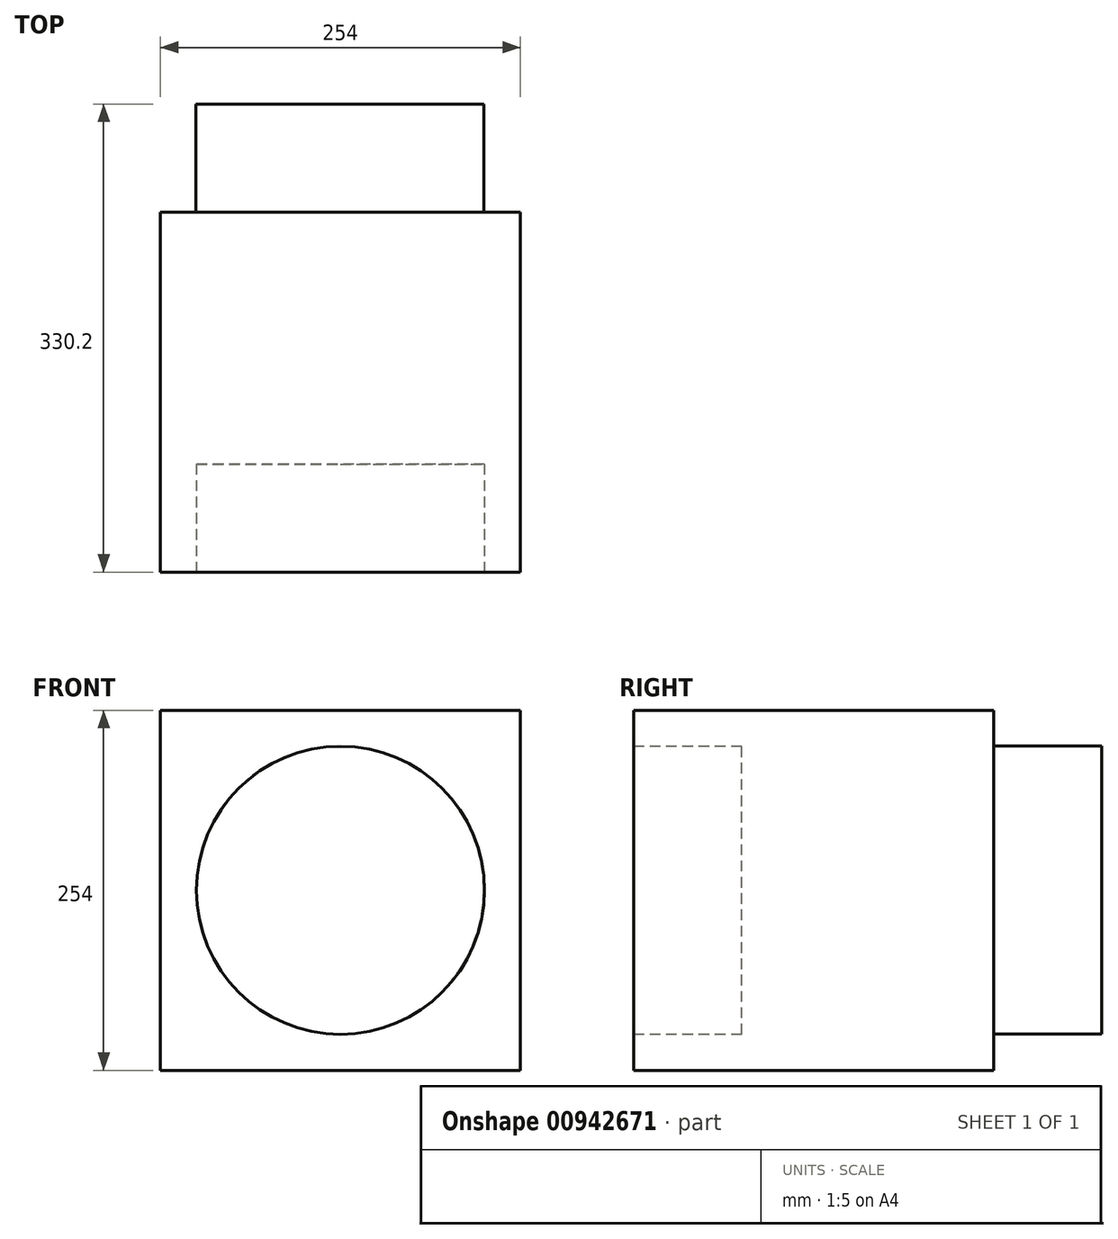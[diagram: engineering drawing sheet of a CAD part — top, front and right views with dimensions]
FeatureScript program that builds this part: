
annotation { "Feature Type Name" : "Feature", "Feature Type Description" : "" }
export const myFeature = defineFeature(function(context is Context, id is Id, definition is map)
    precondition{}
    {
        {
            var Q0;
            Q0=qCreatedBy(makeId("Front.planeOp"),FACE);
            var sketch = newSketch(context, id + "F0", { "sketchPlane" : qUnion([Q0])});
            skLineSegment(sketch, "E0.bottom", {"start": v(-127, 127) * mm, "end": v(127, 127) * mm});
            skLineSegment(sketch, "E0.top", {"start": v(-127, -127) * mm, "end": v(127, -127) * mm});
            skLineSegment(sketch, "E0.left", {"start": v(-127, 127) * mm, "end": v(-127, -127) * mm});
            skLineSegment(sketch, "E0.right", {"start": v(127, 127) * mm, "end": v(127, -127) * mm});
            skPoint(sketch, "E0.middle", {"position": v(0, 0) * mm});
            skSolve(sketch);
        }
        {
            var Q0;
            Q0 = qSketchRegion(id + "F0", true);
            extrude(context, id + "F1", {"entities" : qUnion([Q0]), "depth" : 254 * mm, "offsetDistance" : 25.4 * mm});
        }
        {
            var Q0;
            Q0=makeQuery(id+"F1.opExtrude","CAP_FACE",FACE,{"disambiguationData":[OSD([sQuery(id+"F0.wireOp",EDGE,"E0.bottom"),sQuery(id+"F0.wireOp",EDGE,"E0.top"),sQuery(id+"F0.wireOp",EDGE,"E0.left"),sQuery(id+"F0.wireOp",EDGE,"E0.right")])],"isStart":true});
            var sketch = newSketch(context, id + "F2", { "sketchPlane" : qUnion([Q0])});
            skCircle(sketch, "E1", {"center": v(0.46, 0.15) * mm, "radius": 101.6 * mm});
            skSolve(sketch);
        }
        {
            var Q0;
            Q0=makeQuery(id+"F1.opExtrude","CAP_FACE",FACE,{"disambiguationData":[OSD([sQuery(id+"F0.wireOp",EDGE,"E0.bottom"),sQuery(id+"F0.wireOp",EDGE,"E0.top"),sQuery(id+"F0.wireOp",EDGE,"E0.left"),sQuery(id+"F0.wireOp",EDGE,"E0.right")])],"isStart":false});
            var sketch = newSketch(context, id + "F3", { "sketchPlane" : qUnion([Q0])});
            skCircle(sketch, "E2", {"center": v(0, 0) * mm, "radius": 101.6 * mm});
            skSolve(sketch);
        }
        {
            var Q0;
            Q0=makeQuery(id+"F3.imprint","IMPRINT",FACE,{"disambiguationData":[TD([[makeQuery(id+"F3.imprint","IMPRINT",EDGE,{"derivedFrom":sQuery(id+"F3.wireOp",EDGE,"E2")}),1.0]])]});
            extrude(context, id + "F4", {"entities" : qUnion([Q0]), "operationType" : NewBodyOperationType.REMOVE, "oppositeDirection" : true, "depth" : 76.2 * mm, "offsetDistance" : 25.4 * mm});
        }
        {
            var Q0;
            Q0=makeQuery(id+"F2.imprint","IMPRINT",FACE,{"disambiguationData":[TD([[makeQuery(id+"F2.imprint","IMPRINT",EDGE,{"derivedFrom":sQuery(id+"F2.wireOp",EDGE,"E1")}),1.0]])]});
            var Q1;
            Q1=sQuery(id+"F2.wireOp",EDGE,"E1");
            extrude(context, id + "F5", {"entities" : qUnion([Q0]), "operationType" : NewBodyOperationType.ADD, "surfaceEntities" : qUnion([Q1]), "depth" : 76.2 * mm, "offsetDistance" : 25.4 * mm});
        }
    });
